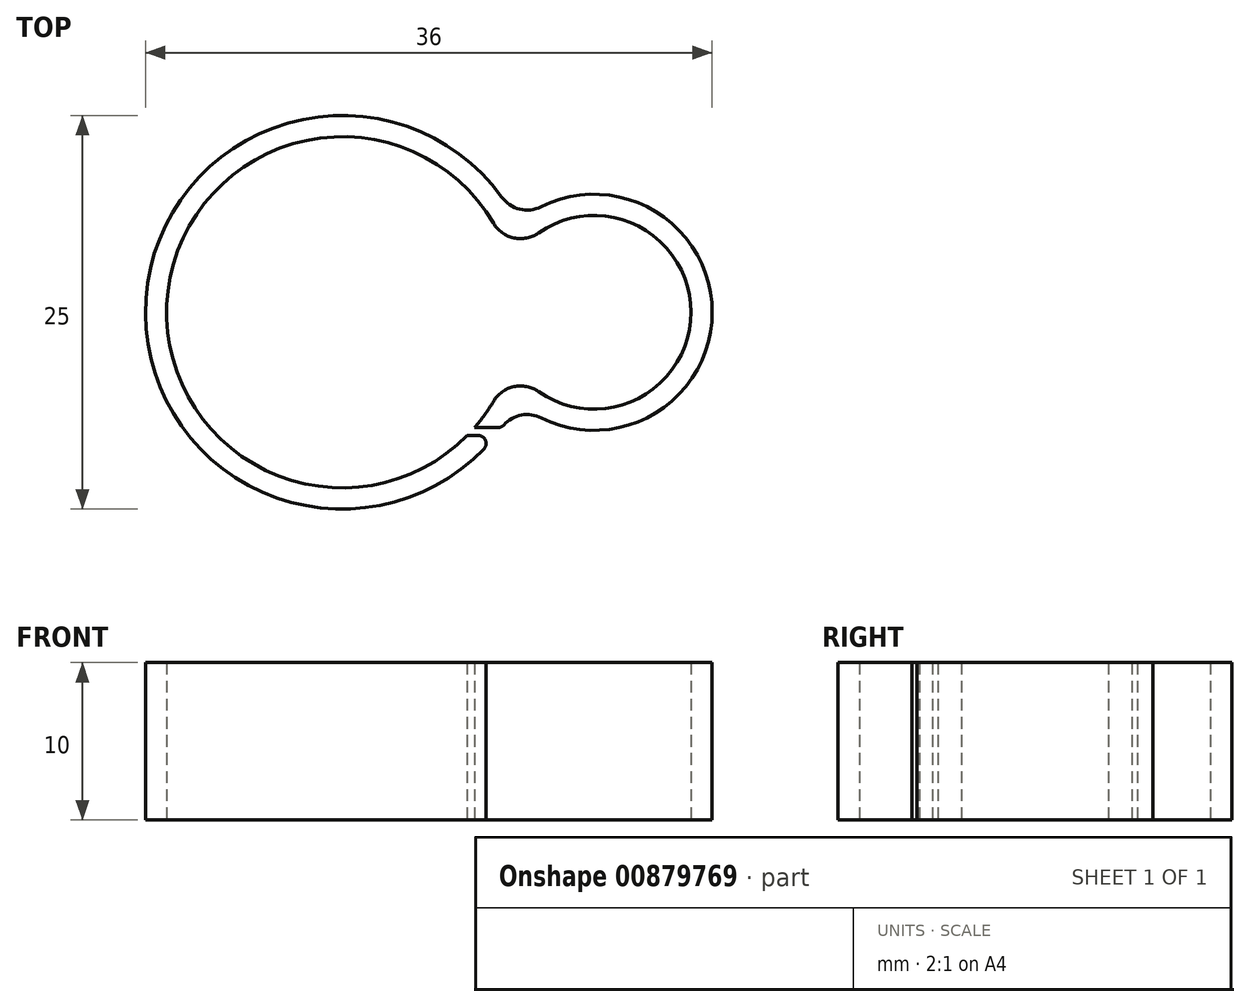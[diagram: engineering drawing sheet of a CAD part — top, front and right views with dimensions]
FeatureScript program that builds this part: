
annotation { "Feature Type Name" : "Feature", "Feature Type Description" : "" }
export const myFeature = defineFeature(function(context is Context, id is Id, definition is map)
    precondition{}
    {
        {
            var Q0;
            Q0=qCreatedBy(makeId("Top.planeOp"),FACE);
            var sketch = newSketch(context, id + "F0", { "sketchPlane" : qUnion([Q0])});
            skArc(sketch, "E0", {"start": v(10.13, 7.32) * mm, "mid": v(-12.5, 0.31) * mm, "end": v(9.75, -7.82) * mm});
            skArc(sketch, "E1", {"start": v(9.6, 5.66) * mm, "mid": v(-11.07, 1.36) * mm, "end": v(7.94, -7.82) * mm});
            skArc(sketch, "E2", {"start": v(12.64, -6.7) * mm, "mid": v(23.5, 0) * mm, "end": v(12.64, 6.7) * mm});
            skArc(sketch, "E3", {"start": v(12.47, -5.04) * mm, "mid": v(22.15, 0) * mm, "end": v(12.47, 5.04) * mm});
            skPoint(sketch, "E4.visualSharp", {"position": v(11.12, 5.7) * mm});
            skArc(sketch, "E4.filletArc", {"start": v(10.13, 7.32) * mm, "mid": v(11.27, 6.55) * mm, "end": v(12.64, 6.7) * mm});
            skPoint(sketch, "E5.visualSharp", {"position": v(10.7, 3.12) * mm});
            skArc(sketch, "E5.filletArc", {"start": v(9.6, 5.66) * mm, "mid": v(10.9, 4.72) * mm, "end": v(12.47, 5.04) * mm});
            skPoint(sketch, "E6.visualSharp", {"position": v(10.7, -3.12) * mm});
            skArc(sketch, "E6.filletArc", {"start": v(12.47, -5.04) * mm, "mid": v(10.9, -4.72) * mm, "end": v(9.6, -5.66) * mm});
            skPoint(sketch, "E7.visualSharp", {"position": v(11.12, -5.7) * mm});
            skArc(sketch, "E7.filletArc", {"start": v(12.64, -6.7) * mm, "mid": v(11.27, -6.55) * mm, "end": v(10.13, -7.32) * mm});
            skLineSegment(sketch, "E8", {"start": v(8.4, -7.32) * mm, "end": v(10.13, -7.32) * mm});
            skLineSegment(sketch, "E9", {"start": v(7.94, -7.82) * mm, "end": v(9.75, -7.82) * mm});
            skArc(sketch, "E10.trimOffspring", {"start": v(8.4, -7.32) * mm, "mid": v(9.04, -6.52) * mm, "end": v(9.6, -5.66) * mm});
            skSolve(sketch);
        }
        {
            var Q0;
            Q0 = qSketchRegion(id + "F0", true);
            extrude(context, id + "F1", {"entities" : qUnion([Q0]), "depth" : 10 * mm, "offsetDistance" : 25 * mm});
        }
        {
            var Q0;
            Q0=makeQuery(id+"F1.opExtrude","SWEPT_EDGE",EDGE,{"disambiguationData":[OSD([sQuery(id+"F0.wireOp",EDGE,"E0"),sQuery(id+"F0.wireOp",EDGE,"E9")])]});
            var Q1;
            Q1=makeQuery(id+"F1.opExtrude","SWEPT_EDGE",EDGE,{"disambiguationData":[OSD([sQuery(id+"F0.wireOp",EDGE,"E7.filletArc"),sQuery(id+"F0.wireOp",EDGE,"E8")])]});
            fillet(context, id + "F2", {"entities" : qUnion([Q0, Q1]), "radius" : .5 * mm, "tangentPropagation" : true, "allowEdgeOverflow" : false});
        }
    });
